# Revit family: LAMP_OCULT DOWNLIGHT RECESSED MEDIUM FLOOD
name_source: partatom
category: Modelos genéricos
revit_build: Autodesk Revit 2015 (Build: 20140606_1530(x64)
units: mm (PartAtom-declared; Revit-internal decimal feet)

## types (20) — shared parameters
CRI = 80
Elevación por defecto = 1219 mm
Fabricante = LAMP
Gear = Adjustable DALI
IEE = A+
Installation instructions = https://www.lamp.es
Insulation class = II
LED Lifetime = 50.000 L90 B10
Lamp = HIGH POWER LED
Last update = 12/02/2019
Luminaire type = Indoor - Downlight
MacAdam = 3
Manufacturer URL = http://www.lamp.es
Manufacturer country = Spain
Manufacturer name = LAMP
Model explanation = Availability of change reflector color when placed in a project.
Photometric web file = Perfil luminico REC MF : 2 MOD 360LM 3000 MEDIUM FLOOD BLACK
Product URL = https://www.lamp.es
Product datasheet = http://www.lamp.es
Protection rating = IP20
Type = HI POWER NICHIA
UGR = 3

## per-type parameters (varying)
| type | Descripción | Dimensions | Efficacy | Finish | Initial color | Initial intensity | Modelo | Number of reflectors | Plum | Power | Power Supply | Product code | Recessed dimensions | Weight |
| 2 MOD 360LM 3000 MEDIUM FLOOD BLACK | OCULT REC 2 400 WW MFL BK/BK. | 83 x 50 x 68 | 72 lm/W | Texturised black | 3000 K | 360 lm | OD1RE204MF830DBB | 2 | 5 W | 4 W | 100-240V 50-60Hz | OD1RE204MF830DBB | 74 x 43 | 0.26 kg |
| 2 MOD 360LM 3000 MEDIUM FLOOD WHITE | OCULT REC 2 400 WW MFL BK/WH. | 83 x 50 x 68 | 72 lm/W | 9010 textured | 3000 K | 360 lm | OD1RE204MF830DBW | 2 | 5 W | 4 W | 100-240V 50-60Hz | OD1RE204MF830DBW | 74 x 43 | 0.26 kg |
| 2 MOD 360LM 4000 MEDIUM FLOOD BLACK | OCULT REC 2 400 NW MFL BK/BK. | 83 x 50 x 68 | 72 lm/W | Texturised black | 4000 K | 360 lm | OD1RE204MF840DBB | 2 | 5 W | 4 W | 100-240V 50-60Hz | OD1RE204MF840DBB | 74 x 43 | 0.26 kg |
| 2 MOD 360LM 4000 MEDIUM FLOOD WHITE | OCULT REC 2 400 NW MFL BK/WH. | 83 x 50 x 68 | 72 lm/W | 9010 textured | 4000 K | 360 lm | OD1RE204MF840DBW | 2 | 5 W | 4 W | 100-240V 50-60Hz | OD1RE204MF840DBW | 74 x 43 | 0.26 kg |
| 3 MOD 540LM 3000 MEDIUM FLOOD BLACK | OCULT REC 3 600 WW MFL BK/BK. | 116 x 50 x 68 | 68 lm/W | Texturised black | 3000 K | 540 lm | OD1RE306MF830DBB | 3 | 8 W | 6 W | 100-240V 50-60Hz | OD1RE306MF830DBB | 107 x 43 | 0.33 kg |
| 3 MOD 540LM 3000 MEDIUM FLOOD WHITE | OCULT REC 3 600 WW MFL BK/WH. | 116 x 50 x 68 | 68 lm/W | 9010 textured | 3000 K | 540 lm | OD1RE306MF830DBW | 3 | 8 W | 6 W | 100-240V 50-60Hz | OD1RE306MF830DBW | 107 x 43 | 0.33 kg |
| 3 MOD 540LM 4000 MEDIUM FLOOD BLACK | OCULT REC 3 600 NW MFL BK/BK. | 116 x 50 x 68 | 68 lm/W | Texturised black | 4000 K | 540 lm | OD1RE306MF840DBB | 3 | 8 W | 6 W | 100-240V 50-60Hz | OD1RE306MF840DBB | 107 x 43 | 0.33 kg |
| 3 MOD 540LM 4000 MEDIUM FLOOD WHITE | OCULT REC 3 600 NW MFL BK/WH. | 116 x 50 x 68 | 68 lm/W | 9010 textured | 4000 K | 540 lm | OD1RE306MF840DBW | 3 | 8 W | 6 W | 100-240V 50-60Hz | OD1RE306MF840DBW | 107 x 43 | 0.33 kg |
| 6 MOD 1080LM 3000 MEDIUM FLOOD BLACK | OCULT REC 6 1200 WW MFL BK/BK. | 215 x 50 x 68 | 77 lm/W | Texturised black | 3000 K | 1080 lm | OD1RE612MF830DBB | 6 | 14 W | 12 W | 220-240V 50-60Hz | OD1RE612MF830DBB | 207 x 43 | 0.61 kg |
| 6 MOD 1080LM 3000 MEDIUM FLOOD WHITE | OCULT REC 6 1200 WW MFL BK/WH. | 215 x 50 x 68 | 77 lm/W | 9010 textured | 3000 K | 1080 lm | OD1RE612MF830DBW | 6 | 14 W | 12 W | 220-240V 50-60Hz | OD1RE612MF830DBW | 207 x 43 | 0.61 kg |
| 6 MOD 1080LM 4000 MEDIUM FLOOD BLACK | OCULT REC 6 1200 NW MFL BK/BK. | 215 x 50 x 68 | 77 lm/W | Texturised black | 4000 K | 1080 lm | OD1RE612MF840DBB | 6 | 14 W | 12 W | 220-240V 50-60Hz | OD1RE612MF840DBB | 207 x 43 | 0.61 kg |
| 6 MOD 1080LM 4000 MEDIUM FLOOD WHITE | OCULT REC 6 1200 NW MFL BK/WH. | 215 x 50 x 68 | 77 lm/W | 9010 textured | 4000 K | 1080 lm | OD1RE612MF840DBW | 6 | 14 W | 12 W | 220-240V 50-60Hz | OD1RE612MF840DBW | 207 x 43 | 0.61 kg |
| 9 MOD 1620LM 3000 MEDIUM FLOOD BLACK | OCULT REC 9 1800 WW MFL BK/BK. | 314 x 50 x 68 | 81 lm/W | Texturised black | 3000 K | 1620 lm | OD1RE918MF830DBB | 9 | 20 W | 18 W | 120-277V 50-60Hz | OD1RE918MF830DBB | 307 x 43 | 0.86 kg |
| 9 MOD 1620LM 3000 MEDIUM FLOOD WHITE | OCULT REC 9 1800 WW MFL BK/WH. | 314 x 50 x 68 | 81 lm/W | 9010 textured | 3000 K | 1620 lm | OD1RE918MF830DBW | 9 | 20 W | 18 W | 120-277V 50-60Hz | OD1RE918MF830DBW | 307 x 43 | 0.86 kg |
| 9 MOD 1620LM 4000 MEDIUM FLOOD BLACK | OCULT REC 9 1800 NW MFL BK/BK. | 314 x 50 x 68 | 81 lm/W | Texturised black | 4000 K | 1620 lm | OD1RE918MF840DBB | 9 | 20 W | 18 W | 120-277V 50-60Hz | OD1RE918MF840DBB | 307 x 43 | 0.86 kg |
| 9 MOD 1620LM 4000 MEDIUM FLOOD WHITE | OCULT REC 9 1800 NW MFL BK/WH. | 314 x 50 x 68 | 81 lm/W | 9010 textured | 4000 K | 1620 lm | OD1RE918MF840DBW | 9 | 20 W | 18 W | 120-277V 50-60Hz | OD1RE918MF840DBW | 307 x 43 | 0.86 kg |
| 12 MOD 2160LM 3000 MEDIUM FLOOD BLACK | OCULT REC 12 2400 WW MFL BK/BK. | 413 x 50 x 68 | 81 lm/W | Texturised black | 3000 K | 2160 lm | OD1RE1222MF830DBB | 12 | 27 W | 24 W | 120-240V 50-60Hz | OD1RE1222MF830DBB | 407 x 43 | 1.14 kg |
| 12 MOD 2160LM 3000 MEDIUM FLOOD WHITE | OCULT REC 12 2400 WW MFL BK/WH. | 413 x 50 x 68 | 81 lm/W | 9010 textured | 3000 K | 2160 lm | OD1RE1222MF830DBW | 12 | 27 W | 24 W | 120-240V 50-60Hz | OD1RE1222MF830DBW | 407 x 43 | 1.14 kg |
| 12 MOD 2160LM 4000 MEDIUM FLOOD BLACK | OCULT REC 12 2400 NW MFL BK/BK. | 413 x 50 x 68 | 81 lm/W | Texturised black | 4000 K | 2160 lm | OD1RE1222MF840DBB | 12 | 27 W | 24 W | 120-240V 50-60Hz | OD1RE1222MF840DBB | 407 x 43 | 1.14 kg |
| 12 MOD 2160LM 4000 MEDIUM FLOOD WHITE | OCULT REC 12 2400 NW MFL BK/WH. | 413 x 50 x 68 | 81 lm/W | 9010 textured | 4000 K | 2160 lm | OD1RE1222MF840DBW | 12 | 27 W | 24 W | 120-240V 50-60Hz | OD1RE1222MF840DBW | 407 x 43 | 1.14 kg |

## geometry (parser evidence)
native form markers: Blend x4
no freeform markers — native parametric forms only
